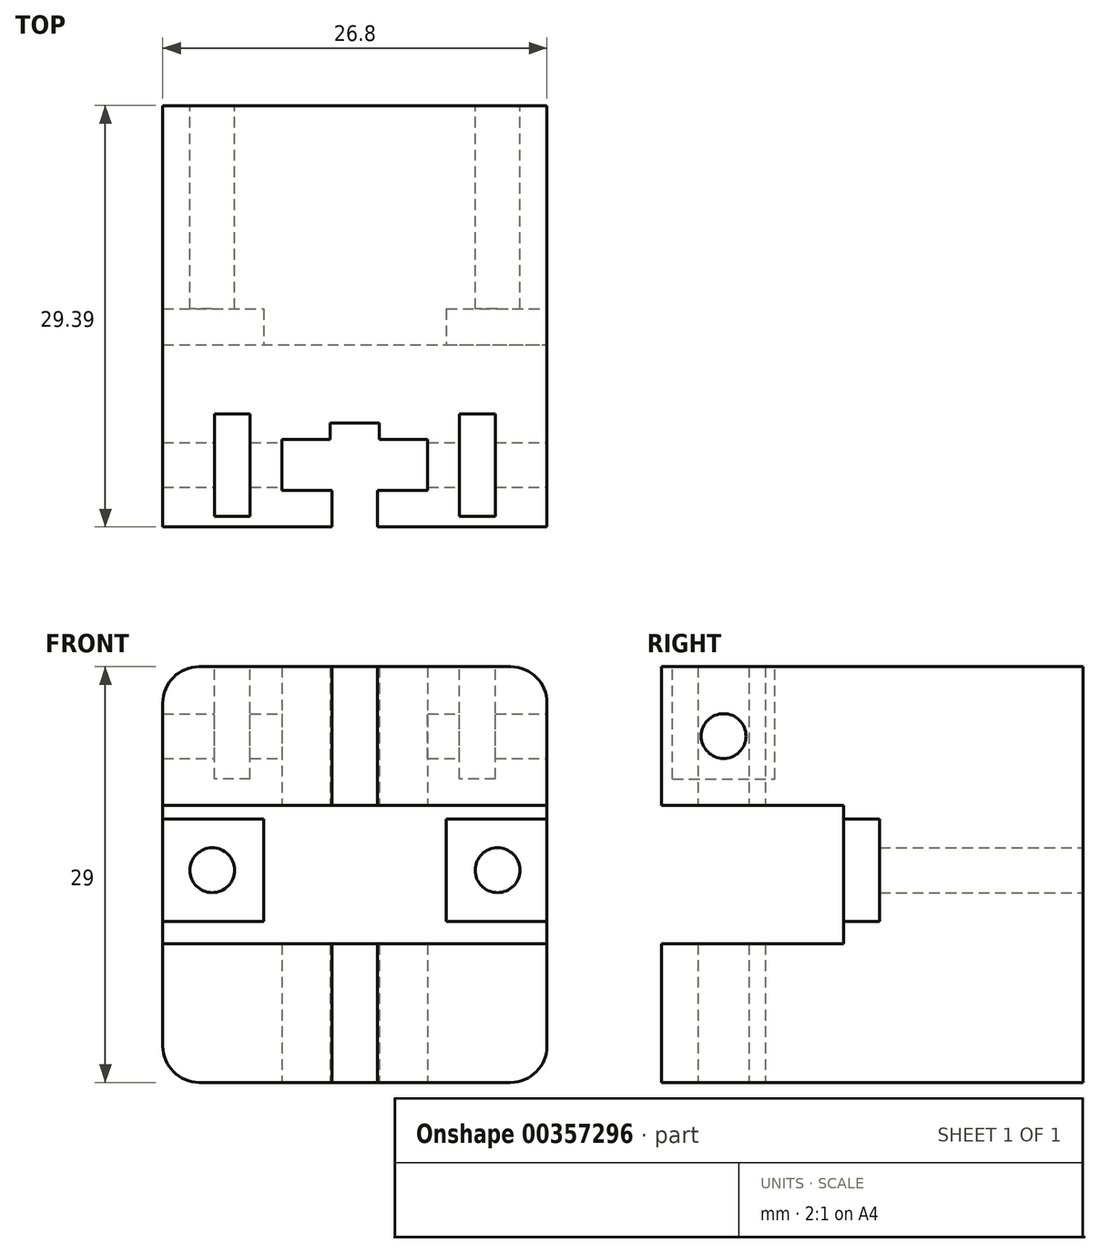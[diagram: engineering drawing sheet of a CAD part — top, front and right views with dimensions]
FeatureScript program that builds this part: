
annotation { "Feature Type Name" : "Feature", "Feature Type Description" : "" }
export const myFeature = defineFeature(function(context is Context, id is Id, definition is map)
    precondition{}
    {
        {
            var Q0;
            Q0=qCreatedBy(makeId("Top.planeOp"),FACE);
            var sketch = newSketch(context, id + "F0", { "sketchPlane" : qUnion([Q0])});
            skLineSegment(sketch, "E0.bottom", {"start": v(0, 0) * mm, "end": v(-26.8, 0) * mm});
            skLineSegment(sketch, "E0.top", {"start": v(0, 29.39) * mm, "end": v(-26.8, 29.39) * mm});
            skLineSegment(sketch, "E0.left", {"start": v(0, 0) * mm, "end": v(0, 29.39) * mm});
            skLineSegment(sketch, "E0.right", {"start": v(-26.8, 0) * mm, "end": v(-26.8, 29.39) * mm});
            skLineSegment(sketch, "E1", {"start": v(-13.4, 29.39) * mm, "end": v(-13.4, 0) * mm, "construction": true});
            skLineSegment(sketch, "E2", {"start": v(-26.8, 14.7) * mm, "end": v(0, 14.7) * mm, "construction": true});
            skLineSegment(sketch, "E3", {"start": v(-15.11, 7.24) * mm, "end": v(-11.69, 7.24) * mm});
            skLineSegment(sketch, "E4", {"start": v(-11.69, 7.24) * mm, "end": v(-11.69, 6.1) * mm});
            skLineSegment(sketch, "E5", {"start": v(-11.69, 6.1) * mm, "end": v(-8.32, 6.1) * mm});
            skLineSegment(sketch, "E6", {"start": v(-8.32, 6.1) * mm, "end": v(-8.32, 2.54) * mm});
            skLineSegment(sketch, "E7", {"start": v(-18.48, 2.54) * mm, "end": v(-18.48, 6.1) * mm});
            skLineSegment(sketch, "E8", {"start": v(-18.48, 6.1) * mm, "end": v(-15.11, 6.1) * mm});
            skLineSegment(sketch, "E9", {"start": v(-15.11, 6.1) * mm, "end": v(-15.11, 7.24) * mm});
            skLineSegment(sketch, "E10", {"start": v(-18.48, 2.54) * mm, "end": v(-14.99, 2.54) * mm});
            skLineSegment(sketch, "E11", {"start": v(-14.99, 2.54) * mm, "end": v(-14.99, 0) * mm});
            skLineSegment(sketch, "E12", {"start": v(-14.99, 0) * mm, "end": v(-11.81, 0) * mm});
            skLineSegment(sketch, "E13", {"start": v(-11.81, 0) * mm, "end": v(-11.81, 2.54) * mm});
            skLineSegment(sketch, "E14", {"start": v(-11.81, 2.54) * mm, "end": v(-8.32, 2.54) * mm});
            skPoint(sketch, "E15", {"position": v(-13.4, 7.24) * mm});
            skLineSegment(sketch, "E16", {"start": v(-14.99, 2.54) * mm, "end": v(-11.81, 2.54) * mm, "construction": true});
            skPoint(sketch, "E17", {"position": v(-13.4, 2.54) * mm});
            skSolve(sketch);
        }
        {
            var Q0;
            Q0=makeQuery(id+"F0.imprint","IMPRINT",FACE,{"disambiguationData":[TD([[makeQuery(id+"F0.imprint","IMPRINT",EDGE,{"derivedFrom":sQuery(id+"F0.wireOp",EDGE,"E0.top")}),1.0]])]});
            extrude(context, id + "F1", {"entities" : qUnion([Q0]), "depth" : 29 * mm});
        }
        {
            var Q0;
            {var subQ0=sQuery(id+"F0.wireOp",EDGE,"E0.bottom");Q0=makeQuery(id+"F1.opExtrude","SWEPT_FACE",FACE,{"disambiguationData":[OSD([subQ0]),TDD([makeQuery(id+"F0.imprint","IMPRINT",EDGE,{"disambiguationData":[TD([[makeQuery(id+"F0.imprint","INTERSECT",VERTEX,{"derivedFrom":[subQ0,sQuery(id+"F0.wireOp",EDGE,"E0.left")]}),-1.0]])],"derivedFrom":subQ0})])]});}
            var sketch = newSketch(context, id + "F2", { "sketchPlane" : qUnion([Q0])});
            skLineSegment(sketch, "E18.bottom", {"start": v(-26.8, 9.67) * mm, "end": v(0, 9.67) * mm});
            skLineSegment(sketch, "E18.top", {"start": v(-26.8, 19.33) * mm, "end": v(0, 19.33) * mm});
            skLineSegment(sketch, "E18.left", {"start": v(-26.8, 9.67) * mm, "end": v(-26.8, 19.33) * mm});
            skLineSegment(sketch, "E18.right", {"start": v(0, 9.67) * mm, "end": v(0, 19.33) * mm});
            skPoint(sketch, "E19", {"position": v(-26.8, 14.5) * mm});
            skSolve(sketch);
        }
        {
            var Q0;
            Q0 = qSketchRegion(id + "F2", true);
            var Q1;
            Q1=makeQuery(id+"F1.opExtrude","SWEPT_FACE",FACE,{"disambiguationData":[OSD([sQuery(id+"F0.wireOp",EDGE,"E8")])]});
            extrude(context, id + "F3", {"entities" : qUnion([Q0]), "operationType" : NewBodyOperationType.REMOVE, "oppositeDirection" : true, "endBoundEntityFace" : qUnion([Q1]), "depth" : 12.7 * mm});
        }
        {
            var Q0;
            Q0=makeQuery(id+"F1.opExtrude","CAP_EDGE",EDGE,{"disambiguationData":[OSD([sQuery(id+"F0.wireOp",EDGE,"E0.left")])],"isStart":false});
            var Q1;
            Q1=makeQuery(id+"F1.opExtrude","CAP_EDGE",EDGE,{"disambiguationData":[OSD([sQuery(id+"F0.wireOp",EDGE,"E0.right")])],"isStart":false});
            var Q2;
            Q2=makeQuery(id+"F1.opExtrude","CAP_EDGE",EDGE,{"disambiguationData":[OSD([sQuery(id+"F0.wireOp",EDGE,"E0.right")])],"isStart":true});
            var Q3;
            Q3=makeQuery(id+"F1.opExtrude","CAP_EDGE",EDGE,{"disambiguationData":[OSD([sQuery(id+"F0.wireOp",EDGE,"E0.left")])],"isStart":true});
            fillet(context, id + "F4", {"entities" : qUnion([Q0, Q1, Q2, Q3]), "radius" : 2.54 * mm, "tangentPropagation" : true, "allowEdgeOverflow" : false});
        }
        {
            var Q0;
            Q0=makeQuery(id+"F1.opExtrude","SWEPT_FACE",FACE,{"disambiguationData":[OSD([sQuery(id+"F0.wireOp",EDGE,"E0.top")])]});
            var sketch = newSketch(context, id + "F5", { "sketchPlane" : qUnion([Q0])});
            skLineSegment(sketch, "E20", {"start": v(3.45, 14.8) * mm, "end": v(23.35, 14.8) * mm, "construction": true});
            skLineSegment(sketch, "E21", {"start": v(13.4, 0) * mm, "end": v(13.4, 29) * mm, "construction": true});
            skPoint(sketch, "E22", {"position": v(13.4, 14.8) * mm});
            skCircle(sketch, "E23", {"center": v(3.45, 14.8) * mm, "radius": 1.56 * mm});
            skCircle(sketch, "E24", {"center": v(23.35, 14.8) * mm, "radius": 1.56 * mm});
            skSolve(sketch);
        }
        {
            var Q0;
            Q0 = qSketchRegion(id + "F5", true);
            extrude(context, id + "F6", {"entities" : qUnion([Q0]), "operationType" : NewBodyOperationType.REMOVE, "endBound" : BoundingType.UP_TO_NEXT, "oppositeDirection" : true, "depth" : 25.4 * mm});
        }
        {
            var Q0;
            Q0=makeQuery(id+"F3.boolean.opBoolean","COPY",FACE,{"derivedFrom":makeQuery(id+"F3.opExtrude","CAP_FACE",FACE,{"disambiguationData":[OSD([sQuery(id+"F2.wireOp",EDGE,"E18.bottom"),sQuery(id+"F2.wireOp",EDGE,"E18.top"),sQuery(id+"F2.wireOp",EDGE,"E18.left"),sQuery(id+"F2.wireOp",EDGE,"E18.right")])],"isStart":false})});
            var sketch = newSketch(context, id + "F7", { "sketchPlane" : qUnion([Q0])});
            skLineSegment(sketch, "E25.bottom", {"start": v(-26.92, 18.37) * mm, "end": v(-19.78, 18.37) * mm});
            skLineSegment(sketch, "E25.top", {"start": v(-26.92, 11.23) * mm, "end": v(-19.78, 11.23) * mm});
            skLineSegment(sketch, "E25.left", {"start": v(-26.92, 18.37) * mm, "end": v(-26.92, 11.23) * mm});
            skLineSegment(sketch, "E25.right", {"start": v(-19.78, 18.37) * mm, "end": v(-19.78, 11.23) * mm});
            skPoint(sketch, "E25.middle", {"position": v(-23.35, 14.8) * mm});
            skLineSegment(sketch, "E26.bottom", {"start": v(-7.02, 18.37) * mm, "end": v(0.12, 18.37) * mm});
            skLineSegment(sketch, "E26.top", {"start": v(-7.02, 11.23) * mm, "end": v(0.12, 11.23) * mm});
            skLineSegment(sketch, "E26.left", {"start": v(-7.02, 18.37) * mm, "end": v(-7.02, 11.23) * mm});
            skLineSegment(sketch, "E26.right", {"start": v(0.12, 18.37) * mm, "end": v(0.12, 11.23) * mm});
            skPoint(sketch, "E26.middle", {"position": v(-3.45, 14.8) * mm});
            skSolve(sketch);
        }
        {
            var Q0;
            Q0 = qSketchRegion(id + "F7", true);
            extrude(context, id + "F8", {"entities" : qUnion([Q0]), "operationType" : NewBodyOperationType.REMOVE, "oppositeDirection" : true, "depth" : 2.5 * mm});
        }
        {
            var Q0;
            Q0=makeQuery(id+"F1.opExtrude","SWEPT_FACE",FACE,{"disambiguationData":[OSD([sQuery(id+"F0.wireOp",EDGE,"E0.right")])]});
            var sketch = newSketch(context, id + "F9", { "sketchPlane" : qUnion([Q0])});
            skLineSegment(sketch, "E27.bottom", {"start": v(-7.89, 27.75) * mm, "end": v(-0.75, 27.75) * mm});
            skLineSegment(sketch, "E27.top", {"start": v(-7.89, 20.6) * mm, "end": v(-0.75, 20.6) * mm});
            skLineSegment(sketch, "E27.left", {"start": v(-7.89, 27.75) * mm, "end": v(-7.89, 20.6) * mm});
            skLineSegment(sketch, "E27.right", {"start": v(-0.75, 27.75) * mm, "end": v(-0.75, 20.6) * mm});
            skPoint(sketch, "E27.middle", {"position": v(-4.32, 24.18) * mm});
            skLineSegment(sketch, "E28", {"start": v(-4.32, 24.18) * mm, "end": v(0, 24.18) * mm, "construction": true});
            skPoint(sketch, "E28.endSnap0", {"position": v(-0.75, 24.18) * mm});
            skSolve(sketch);
        }
        {
            var Q0;
            Q0=makeQuery(id+"F1.opExtrude","SWEPT_FACE",FACE,{"disambiguationData":[OSD([sQuery(id+"F0.wireOp",EDGE,"E0.left")])]});
            var sketch = newSketch(context, id + "F10", { "sketchPlane" : qUnion([Q0])});
            skLineSegment(sketch, "E29.bottom", {"start": v(0.75, 27.73) * mm, "end": v(7.89, 27.73) * mm});
            skLineSegment(sketch, "E29.top", {"start": v(0.75, 20.59) * mm, "end": v(7.89, 20.59) * mm});
            skLineSegment(sketch, "E29.left", {"start": v(0.75, 27.73) * mm, "end": v(0.75, 20.59) * mm});
            skLineSegment(sketch, "E29.right", {"start": v(7.89, 27.73) * mm, "end": v(7.89, 20.59) * mm});
            skPoint(sketch, "E29.middle", {"position": v(4.32, 24.16) * mm});
            skSolve(sketch);
        }
        {
            var Q0;
            {var subQ29=sQuery(id+"F10.wireOp",EDGE,"E29.top");Q0=makeQuery(id+"F10.imprint","IMPRINT",FACE,{"disambiguationData":[TD([[makeQuery(id+"F10.imprint","IMPRINT",EDGE,{"derivedFrom":subQ29}),-1.0]])]});}
            var sketch = newSketch(context, id + "F11", { "sketchPlane" : qUnion([Q0])});
            skCircle(sketch, "E30", {"center": v(4.32, 24.16) * mm, "radius": 1.56 * mm});
            skPoint(sketch, "E30.centerSnap0", {"position": v(7.89, 24.16) * mm});
            skPoint(sketch, "E30.centerSnap1", {"position": v(4.32, 20.59) * mm});
            skLineSegment(sketch, "E31.bottom", {"start": v(0.75, 20.59) * mm, "end": v(7.89, 20.59) * mm, "construction": true});
            skLineSegment(sketch, "E31.top", {"start": v(0.75, 27.73) * mm, "end": v(7.89, 27.73) * mm, "construction": true});
            skLineSegment(sketch, "E31.left", {"start": v(0.75, 20.59) * mm, "end": v(0.75, 27.73) * mm, "construction": true});
            skLineSegment(sketch, "E31.right", {"start": v(7.89, 20.59) * mm, "end": v(7.89, 27.73) * mm, "construction": true});
            skSolve(sketch);
        }
        {
            var Q0;
            Q0 = qSketchRegion(id + "F11", true);
            extrude(context, id + "F12", {"entities" : qUnion([Q0]), "operationType" : NewBodyOperationType.REMOVE, "endBound" : BoundingType.THROUGH_ALL, "oppositeDirection" : true, "depth" : 25.4 * mm});
        }
        {
            var Q0;
            Q0=qCreatedBy(makeId("Front.planeOp"),FACE);
            cPlane(context, id + "F13", {"entities" : qUnion([Q0]), "cplaneType" : CPlaneType.OFFSET, "offset" : 10.16 * mm, "oppositeDirection" : true, "width" : 152.4 * mm, "height" : 152.4 * mm});
        }
        {
            var Q0;
            Q0=qCreatedBy(id+"F13.planeOp",FACE);
            var sketch = newSketch(context, id + "F14", { "sketchPlane" : qUnion([Q0])});
            skLineSegment(sketch, "E32.bottom", {"start": v(-33, 32.08) * mm, "end": v(5.71, 32.08) * mm});
            skLineSegment(sketch, "E32.top", {"start": v(-33, -3.32) * mm, "end": v(5.71, -3.32) * mm});
            skLineSegment(sketch, "E32.left", {"start": v(-33, 32.08) * mm, "end": v(-33, -3.32) * mm});
            skLineSegment(sketch, "E32.right", {"start": v(5.71, 32.08) * mm, "end": v(5.71, -3.32) * mm});
            skPoint(sketch, "E32.middle", {"position": v(-13.64, 14.38) * mm});
            skSolve(sketch);
        }
        {
            var Q0;
            Q0=makeQuery(id+"F1.opExtrude","CAP_FACE",FACE,{"disambiguationData":[OSD([sQuery(id+"F0.wireOp",EDGE,"E0.bottom"),sQuery(id+"F0.wireOp",EDGE,"E0.top"),sQuery(id+"F0.wireOp",EDGE,"E0.left"),sQuery(id+"F0.wireOp",EDGE,"E0.right"),sQuery(id+"F0.wireOp",EDGE,"E3"),sQuery(id+"F0.wireOp",EDGE,"E4"),sQuery(id+"F0.wireOp",EDGE,"E5"),sQuery(id+"F0.wireOp",EDGE,"E6"),sQuery(id+"F0.wireOp",EDGE,"E7"),sQuery(id+"F0.wireOp",EDGE,"E8"),sQuery(id+"F0.wireOp",EDGE,"E9"),sQuery(id+"F0.wireOp",EDGE,"E10"),sQuery(id+"F0.wireOp",EDGE,"E11"),sQuery(id+"F0.wireOp",EDGE,"E13"),sQuery(id+"F0.wireOp",EDGE,"E14")])],"isStart":false});
            var sketch = newSketch(context, id + "F15", { "sketchPlane" : qUnion([Q0])});
            skLineSegment(sketch, "E33.bottom", {"start": v(-3.6, 0.75) * mm, "end": v(-6.1, 0.75) * mm});
            skLineSegment(sketch, "E33.top", {"start": v(-3.6, 7.89) * mm, "end": v(-6.1, 7.89) * mm});
            skLineSegment(sketch, "E33.left", {"start": v(-3.6, 0.75) * mm, "end": v(-3.6, 7.89) * mm});
            skLineSegment(sketch, "E33.right", {"start": v(-6.1, 0.75) * mm, "end": v(-6.1, 7.89) * mm});
            skLineSegment(sketch, "E34.bottom", {"start": v(-20.7, 0.75) * mm, "end": v(-23.2, 0.75) * mm});
            skLineSegment(sketch, "E34.top", {"start": v(-20.7, 7.89) * mm, "end": v(-23.2, 7.89) * mm});
            skLineSegment(sketch, "E34.left", {"start": v(-20.7, 0.75) * mm, "end": v(-20.7, 7.89) * mm});
            skLineSegment(sketch, "E34.right", {"start": v(-23.2, 0.75) * mm, "end": v(-23.2, 7.89) * mm});
            skLineSegment(sketch, "E35", {"start": v(-23.2, 4.32) * mm, "end": v(-3.6, 4.32) * mm, "construction": true});
            skLineSegment(sketch, "E36", {"start": v(-20.7, 7.89) * mm, "end": v(-6.1, 7.89) * mm, "construction": true});
            skLineSegment(sketch, "E37", {"start": v(-13.4, 7.89) * mm, "end": v(-13.4, 4.32) * mm, "construction": true});
            skSolve(sketch);
        }
        {
            var Q0;
            Q0 = qSketchRegion(id + "F15", true);
            extrude(context, id + "F16", {"entities" : qUnion([Q0]), "operationType" : NewBodyOperationType.REMOVE, "oppositeDirection" : true, "depth" : 6.55 * mm + 1.27 * mm});
        }
    });
